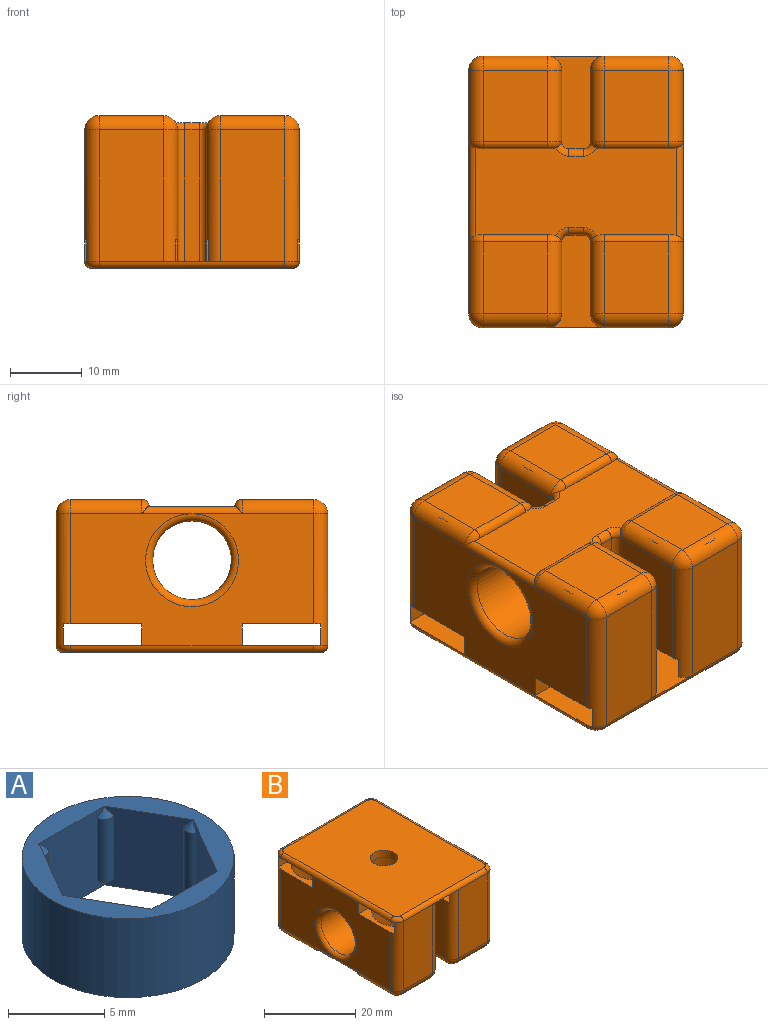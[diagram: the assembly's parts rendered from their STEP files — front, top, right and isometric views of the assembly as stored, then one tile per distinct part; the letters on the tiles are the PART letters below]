
ASSEMBLY  parts=2 mates=1
PART A: 27 faces, bbox 11x11x5 mm
  f0: plane 5x4.15mm, normal (0.87,-0.5,0), area 19.5mm2, adj f7,f8,f21,f22,f23,f24,f25,f26
  f1: plane 5x4.79mm, normal (0,-1,0), area 19.5mm2, adj f7,f8,f9,f10,f11,f21,f22,f23
  f2: plane 5x4.15mm, normal (-0.87,-0.5,0), area 19.5mm2, adj f7,f8,f9,f10,f11,f15,f16,f17
  f3: plane 5x4.15mm, normal (-0.87,0.5,0), area 19.5mm2, adj f7,f8,f12,f13,f14,f15,f16,f17
  f4: plane 5x4.79mm, normal (0,1,0), area 19.5mm2, adj f7,f8,f12,f13,f14,f18,f19,f20
  f5: plane 5x4.15mm, normal (0.87,0.5,0), area 19.5mm2, adj f7,f8,f18,f19,f20,f24,f25,f26
  f6: cylinder r=5.5mm len=11mm, axis (0,0,-1), area 172.8mm2, adj f7,f8
  f7: plane 11x11mm, normal (0,0,1), area 35.4mm2, adj f0,f1,f2,f3,f4,f5,f6
  f8: plane 11x11mm, normal (0,0,-1), area 35.4mm2, adj f0,f1,f2,f3,f4,f5,f6
  f9: cylinder r=0.5mm len=4mm, axis (0,0,-1), area 4.2mm2, adj f1,f2,f10,f11
  f10: cone r=0.5mm half-angle=45deg, axis (0,0,-1), area 0.4mm2, adj f1,f2,f9
  f11: cone r=0.5mm half-angle=45deg, axis (0,0,1), area 0.4mm2, adj f1,f2,f9
  f12: cylinder r=0.5mm len=4mm, axis (0,0,-1), area 4.2mm2, adj f3,f4,f13,f14
  f13: cone r=0.5mm half-angle=45deg, axis (0,0,-1), area 0.4mm2, adj f3,f4,f12
  f14: cone r=0.5mm half-angle=45deg, axis (0,0,1), area 0.4mm2, adj f3,f4,f12
  f15: cylinder r=0.5mm len=4mm, axis (0,0,-1), area 4.2mm2, adj f2,f3,f16,f17
  f16: cone r=0.5mm half-angle=45deg, axis (0,0,-1), area 0.4mm2, adj f2,f3,f15
  f17: cone r=0.5mm half-angle=45deg, axis (0,0,1), area 0.4mm2, adj f2,f3,f15
  f18: cylinder r=0.5mm len=4mm, axis (0,0,-1), area 4.2mm2, adj f4,f5,f19,f20
  f19: cone r=0.5mm half-angle=45deg, axis (0,0,-1), area 0.4mm2, adj f4,f5,f18
  f20: cone r=0.5mm half-angle=45deg, axis (0,0,1), area 0.4mm2, adj f4,f5,f18
  f21: cylinder r=0.5mm len=4mm, axis (0,0,-1), area 4.2mm2, adj f0,f1,f22,f23
  f22: cone r=0.5mm half-angle=45deg, axis (0,0,-1), area 0.4mm2, adj f0,f1,f21
  f23: cone r=0.5mm half-angle=45deg, axis (0,0,1), area 0.4mm2, adj f0,f1,f21
  f24: cylinder r=0.5mm len=4mm, axis (0,0,-1), area 4.2mm2, adj f0,f5,f25,f26
  f25: cone r=0.5mm half-angle=45deg, axis (0,0,-1), area 0.4mm2, adj f0,f5,f24
  f26: cone r=0.5mm half-angle=45deg, axis (0,0,1), area 0.4mm2, adj f0,f5,f24
PART B: 110 faces, bbox 30.3x38.3x21.6 mm
  f0: plane 18.4x9mm, normal (0,-1,0), area 165.6mm2, adj f56,f57,f70,f104
  f1: plane 18.4x9mm, normal (0,1,0), area 165.6mm2, adj f50,f51,f64,f103
  f2: cylinder r=2mm len=10mm, axis (0,1,0), area 31.4mm2, adj f4,f13,f66,f87
  f3: cylinder r=2mm len=10mm, axis (0,1,0), area 31.4mm2, adj f25,f42,f72,f78
  f4: plane 34x18.4mm, normal (-1,0,0), area 432.9mm2, adj f2,f8,f9,f18,f19,f50,f52,f65
  f5: plane 18.4x9mm, normal (0,1,0), area 165.6mm2, adj f54,f55,f73,f103
  f6: plane 15.4x10mm, normal (1,0,0), area 154mm2, adj f11,f51,f60,f90
  f7: cylinder r=5.5mm len=17mm, axis (0,0,1), area 587.5mm2, adj f9,f11,f12
  f8: plane 13x3mm, normal (0,1,0), area 39mm2, adj f4,f9,f11,f14,f90
  f9: plane 11x6.5mm, normal (0,0,1), area 23.9mm2, adj f4,f7,f8,f10,f50
  f10: plane 12.46x3mm, normal (0,-1,0), area 37.4mm2, adj f9,f11,f14,f50,f51
  f11: plane 11x6.5mm, normal (0,0,1), area 23.9mm2, adj f6,f7,f8,f10,f51
  f12: plane 11x11mm, normal (0,0,1), area 95mm2, adj f7
  f13: plane 10x9mm, normal (0,0,-1), area 90mm2, adj f2,f60,f64,f86
  f14: plane 30x13mm, normal (0,0,-1), area 338.9mm2, adj f8,f10,f28,f30,f34,f51,f55,f89
  f15: plane 18.4x9mm, normal (0,-1,0), area 165.6mm2, adj f52,f53,f61,f104
  f16: plane 15.4x10mm, normal (1,0,0), area 154mm2, adj f21,f53,f58,f91
  f17: cylinder r=5.5mm len=17mm, axis (0,0,1), area 587.5mm2, adj f19,f21,f22
  f18: plane 13x3mm, normal (0,-1,0), area 39mm2, adj f4,f19,f21,f24,f91
  f19: plane 11x6.5mm, normal (0,0,1), area 23.9mm2, adj f4,f17,f18,f20,f52
  f20: plane 12.46x3mm, normal (0,1,0), area 37.4mm2, adj f19,f21,f24,f52,f53
  f21: plane 11x6.5mm, normal (0,0,1), area 23.9mm2, adj f16,f17,f18,f20,f53
  f22: plane 11x11mm, normal (0,0,1), area 95mm2, adj f17
  f23: plane 10x9mm, normal (0,0,-1), area 90mm2, adj f58,f61,f65,f83
  f24: plane 30x13mm, normal (0,0,-1), area 338.9mm2, adj f18,f20,f37,f39,f43,f53,f57,f88
  f25: plane 34x18.4mm, normal (1,0,0), area 432.9mm2, adj f3,f28,f29,f37,f38,f54,f56,f74
  f26: plane 15.4x10mm, normal (-1,0,0), area 154mm2, adj f31,f55,f69,f89
  f27: cylinder r=5.5mm len=17mm, axis (0,0,1), area 587.5mm2, adj f29,f31,f32
  f28: plane 13x3mm, normal (0,1,0), area 39mm2, adj f14,f25,f29,f31,f89
  f29: plane 11x6.5mm, normal (0,0,1), area 23.9mm2, adj f25,f27,f28,f30,f54
  f30: plane 12.46x3mm, normal (0,-1,0), area 37.4mm2, adj f14,f29,f31,f54,f55
  f31: plane 11x6.5mm, normal (0,0,1), area 23.9mm2, adj f26,f27,f28,f30,f55
  f32: plane 11x11mm, normal (0,0,1), area 95mm2, adj f27
  f33: plane 10x9mm, normal (0,0,-1), area 90mm2, adj f69,f73,f74,f80
  f34: plane 18.4x2mm, normal (0,1,0), area 36.8mm2, adj f14,f89,f90,f93
  f35: plane 15.4x10mm, normal (-1,0,0), area 154mm2, adj f40,f57,f67,f88
  f36: cylinder r=5.5mm len=17mm, axis (0,0,1), area 587.5mm2, adj f38,f40,f41
  f37: plane 13x3mm, normal (0,-1,0), area 39mm2, adj f24,f25,f38,f40,f88
  f38: plane 11x6.5mm, normal (0,0,1), area 23.9mm2, adj f25,f36,f37,f39,f56
  f39: plane 12.46x3mm, normal (0,1,0), area 37.4mm2, adj f24,f38,f40,f56,f57
  f40: plane 11x6.5mm, normal (0,0,1), area 23.9mm2, adj f35,f36,f37,f39,f57
  f41: plane 11x11mm, normal (0,0,1), area 95mm2, adj f36
  f42: plane 10x9mm, normal (0,0,-1), area 90mm2, adj f3,f67,f70,f77
  f43: plane 18.4x2mm, normal (0,-1,0), area 36.8mm2, adj f24,f88,f91,f96
  f44: plane 28x12.33mm, normal (0,0,-1), area 327.4mm2, adj f76,f77,f78,f79,f80,f81,f82,f83
  f45: cylinder r=5.5mm len=28mm, axis (1,0,0), area 846.6mm2, adj f47,f108,f109
  f46: cylinder r=3mm len=6mm, axis (0,0,1), area 37.7mm2, adj f48,f49
  f47: cylinder r=5.5mm len=11mm, axis (0,0,1), area 255.7mm2, adj f45,f48
  f48: plane 11x11mm, normal (0,0,-1), area 66.8mm2, adj f46,f47
  f49: plane 36x28mm, normal (0,0,1), area 978.9mm2, adj f46,f100,f101,f102,f103,f104,f105,f106
  f50: cylinder r=2mm len=18.4mm, axis (0,0,1), area 54.7mm2, adj f1,f4,f9,f10,f66,f105
  f51: cylinder r=2mm len=18.4mm, axis (0,0,-1), area 54.7mm2, adj f1,f6,f10,f11,f14,f62
  f52: cylinder r=2mm len=18.4mm, axis (0,0,1), area 54.7mm2, adj f4,f15,f19,f20,f63,f106
  f53: cylinder r=2mm len=18.4mm, axis (0,0,-1), area 54.7mm2, adj f15,f16,f20,f21,f24,f59
  f54: cylinder r=2mm len=18.4mm, axis (0,0,1), area 54.7mm2, adj f5,f25,f29,f30,f75,f101
  f55: cylinder r=2mm len=18.4mm, axis (0,0,-1), area 54.7mm2, adj f5,f14,f26,f30,f31,f71
  f56: cylinder r=2mm len=18.4mm, axis (0,0,1), area 54.7mm2, adj f0,f25,f38,f39,f72,f102
  f57: cylinder r=2mm len=18.4mm, axis (0,0,-1), area 54.7mm2, adj f0,f24,f35,f39,f40,f68
  f58: cylinder r=2mm len=10mm, axis (0,-1,0), area 31.4mm2, adj f16,f23,f59,f82
  f59: sphere r=2mm, area 6.3mm2, adj f53,f58,f61
  f60: cylinder r=2mm len=10mm, axis (0,1,0), area 31.4mm2, adj f6,f13,f62,f85
  f61: cylinder r=2mm len=9mm, axis (-1,0,0), area 28.3mm2, adj f15,f23,f59,f63
  f62: sphere r=2mm, area 6.3mm2, adj f51,f60,f64
  f63: sphere r=2mm, area 6.3mm2, adj f52,f61,f65
  f64: cylinder r=2mm len=9mm, axis (-1,0,0), area 28.3mm2, adj f1,f13,f62,f66
  f65: cylinder r=2mm len=10mm, axis (0,1,0), area 31.4mm2, adj f4,f23,f63,f84
  f66: sphere r=2mm, area 6.3mm2, adj f2,f50,f64
  f67: cylinder r=2mm len=10mm, axis (0,-1,0), area 31.4mm2, adj f35,f42,f68,f76
  f68: sphere r=2mm, area 6.3mm2, adj f57,f67,f70
  f69: cylinder r=2mm len=10mm, axis (0,1,0), area 31.4mm2, adj f26,f33,f71,f79
  f70: cylinder r=2mm len=9mm, axis (1,0,0), area 28.3mm2, adj f0,f42,f68,f72
  f71: sphere r=2mm, area 6.3mm2, adj f55,f69,f73
  f72: sphere r=2mm, area 6.3mm2, adj f3,f56,f70
  f73: cylinder r=2mm len=9mm, axis (1,0,0), area 28.3mm2, adj f5,f33,f71,f75
  f74: cylinder r=2mm len=10mm, axis (0,1,0), area 31.4mm2, adj f25,f33,f75,f81
  f75: sphere r=2mm, area 6.3mm2, adj f54,f73,f74
  f76: torus R=1mm, axis (0,1,0), area 2.6mm2, adj f44,f67,f77,f97
  f77: cylinder r=1mm len=9mm, axis (-1,0,0), area 14.1mm2, adj f42,f44,f76,f78
  f78: torus R=1mm, axis (0,1,0), area 2.8mm2, adj f3,f44,f77,f98
  f79: torus R=1mm, axis (0,-1,0), area 2.6mm2, adj f44,f69,f80,f94
  f80: cylinder r=1mm len=9mm, axis (-1,0,0), area 14.1mm2, adj f33,f44,f79,f81
  f81: torus R=1mm, axis (0,-1,0), area 2.8mm2, adj f44,f74,f80,f98
  f82: torus R=1mm, axis (0,1,0), area 2.6mm2, adj f44,f58,f83,f95
  f83: cylinder r=1mm len=9mm, axis (1,0,0), area 14.1mm2, adj f23,f44,f82,f84
  f84: torus R=1mm, axis (0,1,0), area 2.8mm2, adj f44,f65,f83,f99
  f85: torus R=1mm, axis (0,-1,0), area 2.6mm2, adj f44,f60,f86,f92
  f86: cylinder r=1mm len=9mm, axis (1,0,0), area 14.1mm2, adj f13,f44,f85,f87
  f87: torus R=1mm, axis (0,-1,0), area 2.8mm2, adj f2,f44,f86,f99
  f88: cylinder r=1mm len=18.4mm, axis (0,0,1), area 28.9mm2, adj f24,f35,f37,f43,f97
  f89: cylinder r=1mm len=18.4mm, axis (0,0,-1), area 28.9mm2, adj f14,f26,f28,f34,f94
  f90: cylinder r=1mm len=18.4mm, axis (0,0,-1), area 28.9mm2, adj f6,f8,f14,f34,f92
  f91: cylinder r=1mm len=18.4mm, axis (0,0,1), area 28.9mm2, adj f16,f18,f24,f43,f95
  f92: torus R=2mm, axis (0,0,-1), area 2.7mm2, adj f44,f85,f90,f93
  f93: cylinder r=1mm len=2mm, axis (-1,0,0), area 3.1mm2, adj f34,f44,f92,f94
  f94: torus R=2mm, axis (0,0,-1), area 2.7mm2, adj f44,f79,f89,f93
  f95: torus R=2mm, axis (0,0,-1), area 2.7mm2, adj f44,f82,f91,f96
  f96: cylinder r=1mm len=2mm, axis (1,0,0), area 3.1mm2, adj f43,f44,f95,f97
  f97: torus R=2mm, axis (0,0,-1), area 2.7mm2, adj f44,f76,f88,f96
  f98: cylinder r=1mm len=14mm, axis (0,1,0), area 20.6mm2, adj f25,f44,f78,f81
  f99: cylinder r=1mm len=14mm, axis (0,1,0), area 20.6mm2, adj f4,f44,f84,f87
  f100: cylinder r=1mm len=34mm, axis (0,1,0), area 53.4mm2, adj f14,f24,f25,f49,f101,f102
  f101: torus R=1mm, axis (0,0,1), area 4mm2, adj f14,f49,f54,f100,f103
  f102: torus R=1mm, axis (0,0,1), area 4mm2, adj f24,f49,f56,f100,f104
  f103: cylinder r=1mm len=26mm, axis (1,0,0), area 40.8mm2, adj f1,f5,f14,f49,f101,f105
  f104: cylinder r=1mm len=26mm, axis (1,0,0), area 40.8mm2, adj f0,f15,f24,f49,f102,f106
  f105: torus R=1mm, axis (0,0,1), area 4mm2, adj f14,f49,f50,f103,f107
  f106: torus R=1mm, axis (0,0,1), area 4mm2, adj f24,f49,f52,f104,f107
  f107: cylinder r=1mm len=34mm, axis (0,1,0), area 53.4mm2, adj f4,f14,f24,f49,f105,f106
  f108: torus R=6.5mm, axis (1,0,0), area 57.9mm2, adj f4,f45
  f109: torus R=6.5mm, axis (-1,0,0), area 57.9mm2, adj f25,f45
PLACE A t=(-10.22,-0.58,-60.02)mm
PLACE B rot(axis=(1,0,0),180deg) t=(-10.22,-0.58,-61.02)mm
MATE fastened B.f47 <-> A.f6  axis (0,0,1) through (-10.22,-0.58,-60.02)mm
